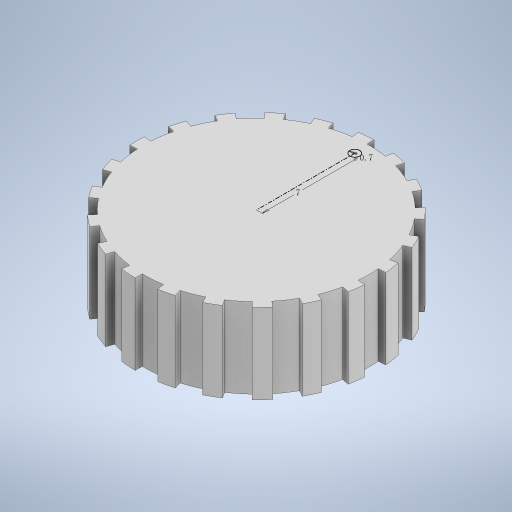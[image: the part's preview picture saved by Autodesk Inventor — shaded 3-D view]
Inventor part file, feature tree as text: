
AUTODESK INVENTOR PART (.ipt)
format: ipt  version: 2023 (Build 270158000, 158)  size: 383,488 bytes
history: native  units: mm
features: sketch x5, extrude x4
ambient origin geometry x8: Origin, YZ Plane, XZ Plane, XY Plane, X Axis, Y Axis, Z Axis, Center Point
bodies: 实体1 (feature_tree)
feature tree (9):
  extrude  "拉伸1"  Depth=2.1mm
  extrude  "拉伸2"  Depth=2.3mm TaperAngle=0.0deg
  sketch  "草图5"  dims[d5=0.4mm d6=0.0mm d27=0.7mm]
  extrude  "拉伸7"  Depth=0.4mm
  extrude  "拉伸6"  Depth=0.5mm
  sketch  "草图1"  dims[d0=3.4mm d1=2.1mm]
  sketch  "草图2"  dims[d2=16.0mm d3=2.3mm d4=0.0mm]
  sketch  "草图6"  dims[d28=7.0mm d31=0.5mm]
  sketch  "草图7"  dims[d32=1.22173mm d33=210.0mm d35=360.0deg d37=0.4mm d38=0.0mm d39=12.7mm d40=3.0mm d41=0.0mm]
